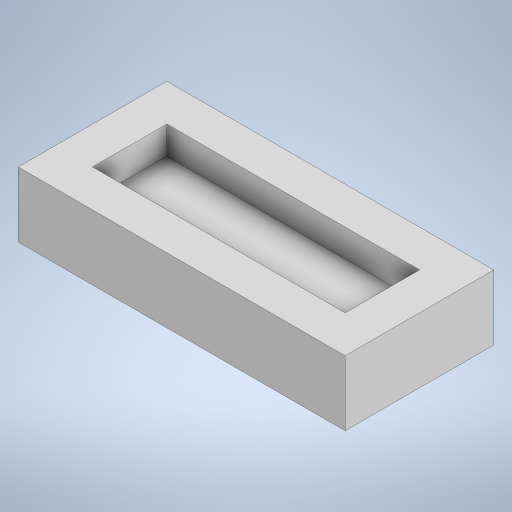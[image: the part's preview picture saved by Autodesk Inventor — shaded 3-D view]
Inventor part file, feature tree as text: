
AUTODESK INVENTOR PART (.ipt)
format: ipt  version: 2024 (Build 280153000, 153)  size: 248,832 bytes
history: native  units: in
note: dims shown in document units (in); Inventor stores cm internally (conversion verified against a paired STEP export)
features: extrude x2, sketch x2
ambient origin geometry x8: Origin, YZ Plane, XZ Plane, XY Plane, X Axis, Y Axis, Z Axis, Center Point
bodies: Solid1 (feature_tree)
feature tree (4):
  extrude  "Extrusion1"  Depth=0.6929in
  extrude  "Extrusion2"  Depth=0.1575in
  sketch  "Sketch1"  dims[d0=0.315in d1=0.6929in]
  sketch  "Sketch2"  dims[d2=0.1378in d3=0.0in d4=0.1575in d5=0.0787in d6=0.0591in d7=0.0in]
